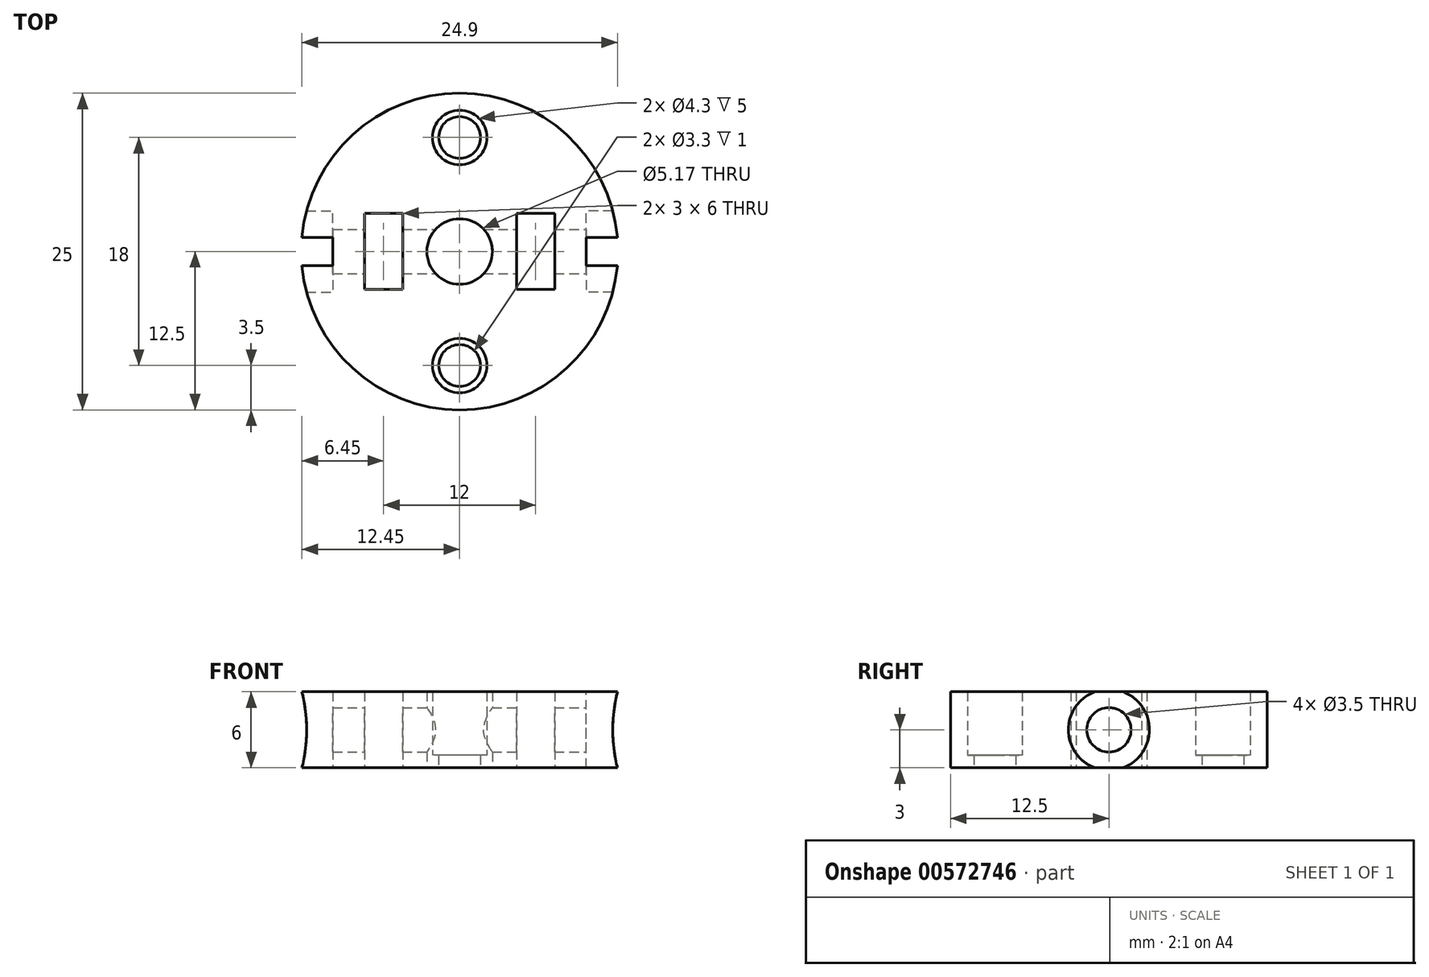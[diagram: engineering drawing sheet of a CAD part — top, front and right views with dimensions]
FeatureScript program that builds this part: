
annotation { "Feature Type Name" : "Feature", "Feature Type Description" : "" }
export const myFeature = defineFeature(function(context is Context, id is Id, definition is map)
    precondition{}
    {
        {
            var Q0;
            Q0=qCreatedBy(makeId("Top.planeOp"),FACE);
            var sketch = newSketch(context, id + "F0", { "sketchPlane" : qUnion([Q0])});
            skCircle(sketch, "E0", {"center": v(0, 0) * mm, "radius": 12.5 * mm});
            skCircle(sketch, "E1", {"center": v(0, 0) * mm, "radius": 2.58 * mm});
            skCircle(sketch, "E2", {"center": v(0, 9) * mm, "radius": 1.65 * mm});
            skCircle(sketch, "E3", {"center": v(0, -9) * mm, "radius": 1.65 * mm});
            skCircle(sketch, "E4", {"center": v(0, 9) * mm, "radius": 2.15 * mm});
            skCircle(sketch, "E5", {"center": v(0, -9) * mm, "radius": 2.15 * mm});
            skLineSegment(sketch, "E6.bottom", {"start": v(-4.5, 3) * mm, "end": v(-7.5, 3) * mm});
            skLineSegment(sketch, "E6.top", {"start": v(-4.5, -3) * mm, "end": v(-7.5, -3) * mm});
            skLineSegment(sketch, "E6.left", {"start": v(-4.5, 3) * mm, "end": v(-4.5, -3) * mm});
            skLineSegment(sketch, "E6.right", {"start": v(-7.5, 3) * mm, "end": v(-7.5, -3) * mm});
            skPoint(sketch, "E6.middle", {"position": v(-6, 0) * mm});
            skLineSegment(sketch, "E7.bottom", {"start": v(7.5, 3) * mm, "end": v(4.5, 3) * mm});
            skLineSegment(sketch, "E7.top", {"start": v(7.5, -3) * mm, "end": v(4.5, -3) * mm});
            skLineSegment(sketch, "E7.left", {"start": v(7.5, 3) * mm, "end": v(7.5, -3) * mm});
            skLineSegment(sketch, "E7.right", {"start": v(4.5, 3) * mm, "end": v(4.5, -3) * mm});
            skPoint(sketch, "E7.middle", {"position": v(6, 0) * mm});
            skSolve(sketch);
        }
        {
            var Q0;
            Q0 = qSketchRegion(id + "F0", true);
            var Q1;
            Q1=makeQuery(id+"F0.imprint","IMPRINT",FACE,{"disambiguationData":[TD([[makeQuery(id+"F0.imprint","IMPRINT",EDGE,{"derivedFrom":sQuery(id+"F0.wireOp",EDGE,"E0")}),1.0]])]});
            extrude(context, id + "F1", {"entities" : qUnion([Q0, Q1]), "depth" : 6 * mm, "offsetDistance" : 25 * mm});
        }
        {
            var Q0;
            Q0=makeQuery(id+"F0.imprint","IMPRINT",FACE,{"disambiguationData":[TD([[makeQuery(id+"F0.imprint","IMPRINT",EDGE,{"derivedFrom":sQuery(id+"F0.wireOp",EDGE,"E2")}),-1.0]])]});
            var Q1;
            Q1=makeQuery(id+"F0.imprint","IMPRINT",FACE,{"disambiguationData":[TD([[makeQuery(id+"F0.imprint","IMPRINT",EDGE,{"derivedFrom":sQuery(id+"F0.wireOp",EDGE,"E3")}),-1.0]])]});
            extrude(context, id + "F2", {"entities" : qUnion([Q0, Q1]), "operationType" : NewBodyOperationType.ADD, "depth" : 1 * mm, "offsetDistance" : 25 * mm});
        }
        {
            var Q0;
            Q0=qCreatedBy(makeId("Right.planeOp"),FACE);
            var sketch = newSketch(context, id + "F3", { "sketchPlane" : qUnion([Q0])});
            skCircle(sketch, "E8", {"center": v(0, 3) * mm, "radius": 1.75 * mm});
            skCircle(sketch, "E9", {"center": v(0, 3) * mm, "radius": 3.2 * mm});
            skSolve(sketch);
        }
        {
            var Q0;
            Q0=makeQuery(id+"F3.imprint","IMPRINT",FACE,{"disambiguationData":[TD([[makeQuery(id+"F3.imprint","IMPRINT",EDGE,{"derivedFrom":sQuery(id+"F3.wireOp",EDGE,"E8")}),1.0]])]});
            extrude(context, id + "F4", {"entities" : qUnion([Q0]), "operationType" : NewBodyOperationType.REMOVE, "endBound" : BoundingType.SYMMETRIC, "oppositeDirection" : true, "depth" : 25 * mm, "offsetDistance" : 25 * mm});
        }
        {
            var Q0;
            Q0 = qSketchRegion(id + "F3", true);
            extrude(context, id + "F5", {"entities" : qUnion([Q0]), "operationType" : NewBodyOperationType.REMOVE, "oppositeDirection" : true, "depth" : 25 * mm, "offsetDistance" : 25 * mm, "hasSecondDirection" : true, "secondDirectionOppositeDirection" : true, "secondDirectionDepth" : 10 * mm});
        }
        {
            var Q0;
            Q0=makeQuery(id+"F3.imprint","IMPRINT",FACE,{"disambiguationData":[TD([[makeQuery(id+"F3.imprint","IMPRINT",EDGE,{"derivedFrom":sQuery(id+"F3.wireOp",EDGE,"E8")}),-1.0]])]});
            extrude(context, id + "F6", {"entities" : qUnion([Q0]), "operationType" : NewBodyOperationType.REMOVE, "depth" : 25 * mm, "offsetDistance" : 25 * mm, "hasSecondDirection" : true, "secondDirectionOppositeDirection" : false, "secondDirectionDepth" : 10 * mm});
        }
    });
